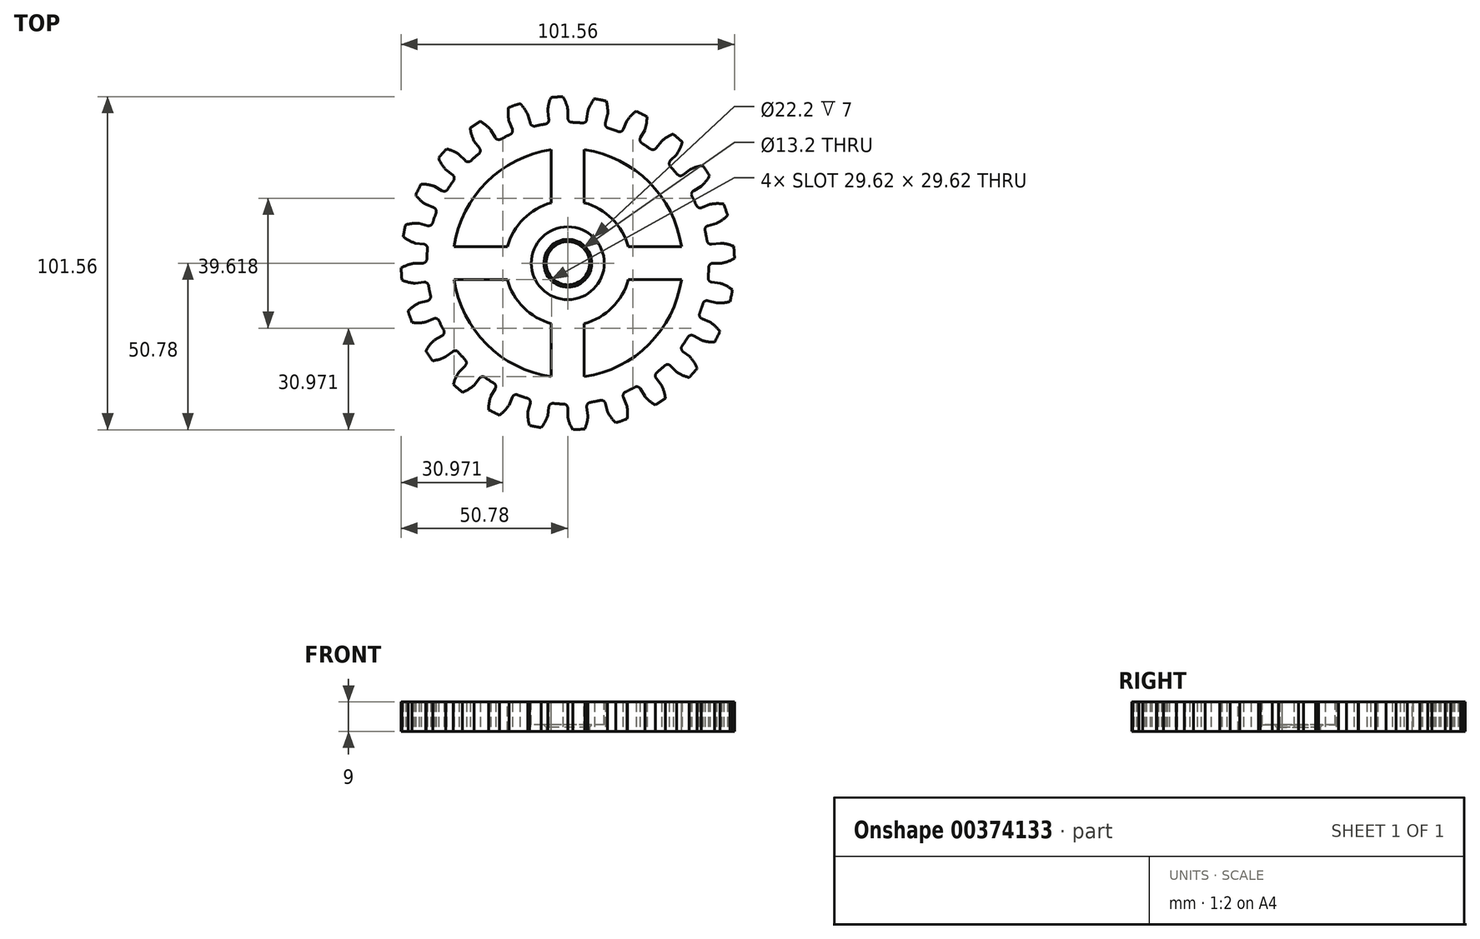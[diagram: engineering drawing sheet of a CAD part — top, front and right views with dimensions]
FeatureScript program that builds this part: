
annotation { "Feature Type Name" : "Feature", "Feature Type Description" : "" }
export const myFeature = defineFeature(function(context is Context, id is Id, definition is map)
    precondition{}
    {
        {
            var Q0;
            Q0=qCreatedBy(makeId("Top.planeOp"),FACE);
            var sketch = newSketch(context, id + "F0", { "sketchPlane" : qUnion([Q0])});
            skArc(sketch, "E0", {"start": v(-1.49, 50.78) * mm, "mid": v(-3.32, 50.7) * mm, "end": v(-5.15, 50.54) * mm});
            skCircle(sketch, "E1", {"center": v(0, 0) * mm, "radius": 42.98 * mm});
            skLineSegment(sketch, "E2", {"start": v(0, 42.98) * mm, "end": v(0, 46.89) * mm});
            skLineSegment(sketch, "E3", {"start": v(-5.6, 42.6) * mm, "end": v(-6.12, 46.49) * mm});
            skArc(sketch, "E4.trimOffspring", {"start": v(0, 46.89) * mm, "mid": v(-0.57, 48.9) * mm, "end": v(-1.49, 50.78) * mm});
            skArc(sketch, "E5.MirrorCS", {"start": v(-6.12, 46.49) * mm, "mid": v(-5.82, 48.56) * mm, "end": v(-5.15, 50.54) * mm});
            skArc(sketch, "E6.1.0", {"start": v(-12.14, 45.3) * mm, "mid": v(-13.2, 47.09) * mm, "end": v(-14.58, 48.66) * mm});
            skArc(sketch, "E6.1.1", {"start": v(-14.58, 48.66) * mm, "mid": v(-16.33, 48.1) * mm, "end": v(-18.06, 47.48) * mm});
            skArc(sketch, "E6.1.2", {"start": v(-17.94, 43.32) * mm, "mid": v(-18.19, 45.4) * mm, "end": v(-18.06, 47.48) * mm});
            skLineSegment(sketch, "E6.1.3", {"start": v(-11.12, 41.51) * mm, "end": v(-12.14, 45.3) * mm});
            skLineSegment(sketch, "E6.1.4", {"start": v(-16.45, 39.7) * mm, "end": v(-17.94, 43.32) * mm});
            skArc(sketch, "E6.2.0", {"start": v(-23.44, 40.6) * mm, "mid": v(-24.94, 42.06) * mm, "end": v(-26.68, 43.23) * mm});
            skArc(sketch, "E6.2.1", {"start": v(-26.68, 43.23) * mm, "mid": v(-28.22, 42.24) * mm, "end": v(-29.73, 41.19) * mm});
            skArc(sketch, "E6.2.2", {"start": v(-28.54, 37.2) * mm, "mid": v(-29.32, 39.14) * mm, "end": v(-29.73, 41.19) * mm});
            skLineSegment(sketch, "E6.2.3", {"start": v(-21.49, 37.22) * mm, "end": v(-23.44, 40.6) * mm});
            skLineSegment(sketch, "E6.2.4", {"start": v(-26.16, 34.1) * mm, "end": v(-28.54, 37.2) * mm});
            skArc(sketch, "E6.3.0", {"start": v(-33.16, 33.16) * mm, "mid": v(-34.98, 34.18) * mm, "end": v(-36.96, 34.85) * mm});
            skArc(sketch, "E6.3.1", {"start": v(-36.96, 34.85) * mm, "mid": v(-38.2, 33.5) * mm, "end": v(-39.38, 32.1) * mm});
            skArc(sketch, "E6.3.2", {"start": v(-37.2, 28.54) * mm, "mid": v(-38.45, 30.22) * mm, "end": v(-39.38, 32.1) * mm});
            skLineSegment(sketch, "E6.3.3", {"start": v(-30.39, 30.39) * mm, "end": v(-33.16, 33.16) * mm});
            skLineSegment(sketch, "E6.3.4", {"start": v(-34.1, 26.16) * mm, "end": v(-37.2, 28.54) * mm});
            skArc(sketch, "E6.4.0", {"start": v(-40.6, 23.44) * mm, "mid": v(-42.63, 23.96) * mm, "end": v(-44.72, 24.1) * mm});
            skArc(sketch, "E6.4.1", {"start": v(-44.72, 24.1) * mm, "mid": v(-45.56, 22.47) * mm, "end": v(-46.34, 20.8) * mm});
            skArc(sketch, "E6.4.2", {"start": v(-43.32, 17.94) * mm, "mid": v(-44.96, 19.24) * mm, "end": v(-46.34, 20.8) * mm});
            skLineSegment(sketch, "E6.4.3", {"start": v(-37.22, 21.49) * mm, "end": v(-40.6, 23.44) * mm});
            skLineSegment(sketch, "E6.4.4", {"start": v(-39.7, 16.45) * mm, "end": v(-43.32, 17.94) * mm});
            skArc(sketch, "E6.5.0", {"start": v(-45.3, 12.14) * mm, "mid": v(-47.38, 12.1) * mm, "end": v(-49.43, 11.7) * mm});
            skArc(sketch, "E6.5.1", {"start": v(-49.43, 11.7) * mm, "mid": v(-49.82, 9.91) * mm, "end": v(-50.15, 8.1) * mm});
            skArc(sketch, "E6.5.2", {"start": v(-46.49, 6.12) * mm, "mid": v(-48.4, 6.95) * mm, "end": v(-50.15, 8.1) * mm});
            skLineSegment(sketch, "E6.5.3", {"start": v(-41.51, 11.12) * mm, "end": v(-45.3, 12.14) * mm});
            skLineSegment(sketch, "E6.5.4", {"start": v(-42.6, 5.6) * mm, "end": v(-46.49, 6.12) * mm});
            skArc(sketch, "E6.6.0", {"start": v(-46.89, 0) * mm, "mid": v(-48.9, -0.57) * mm, "end": v(-50.78, -1.49) * mm});
            skArc(sketch, "E6.6.1", {"start": v(-50.78, -1.49) * mm, "mid": v(-50.7, -3.32) * mm, "end": v(-50.54, -5.15) * mm});
            skArc(sketch, "E6.6.2", {"start": v(-46.49, -6.12) * mm, "mid": v(-48.56, -5.82) * mm, "end": v(-50.54, -5.15) * mm});
            skLineSegment(sketch, "E6.6.3", {"start": v(-42.98, 0) * mm, "end": v(-46.89, 0) * mm});
            skLineSegment(sketch, "E6.6.4", {"start": v(-42.6, -5.6) * mm, "end": v(-46.49, -6.12) * mm});
            skArc(sketch, "E6.7.0", {"start": v(-45.3, -12.14) * mm, "mid": v(-47.09, -13.2) * mm, "end": v(-48.66, -14.58) * mm});
            skArc(sketch, "E6.7.1", {"start": v(-48.66, -14.58) * mm, "mid": v(-48.1, -16.33) * mm, "end": v(-47.48, -18.06) * mm});
            skArc(sketch, "E6.7.2", {"start": v(-43.32, -17.94) * mm, "mid": v(-45.4, -18.19) * mm, "end": v(-47.48, -18.06) * mm});
            skLineSegment(sketch, "E6.7.3", {"start": v(-41.51, -11.12) * mm, "end": v(-45.3, -12.14) * mm});
            skLineSegment(sketch, "E6.7.4", {"start": v(-39.7, -16.45) * mm, "end": v(-43.32, -17.94) * mm});
            skArc(sketch, "E6.8.0", {"start": v(-40.6, -23.44) * mm, "mid": v(-42.06, -24.94) * mm, "end": v(-43.23, -26.68) * mm});
            skArc(sketch, "E6.8.1", {"start": v(-43.23, -26.68) * mm, "mid": v(-42.24, -28.22) * mm, "end": v(-41.19, -29.73) * mm});
            skArc(sketch, "E6.8.2", {"start": v(-37.2, -28.54) * mm, "mid": v(-39.14, -29.32) * mm, "end": v(-41.19, -29.73) * mm});
            skLineSegment(sketch, "E6.8.3", {"start": v(-37.22, -21.49) * mm, "end": v(-40.6, -23.44) * mm});
            skLineSegment(sketch, "E6.8.4", {"start": v(-34.1, -26.16) * mm, "end": v(-37.2, -28.54) * mm});
            skArc(sketch, "E6.9.0", {"start": v(-33.16, -33.16) * mm, "mid": v(-34.18, -34.98) * mm, "end": v(-34.85, -36.96) * mm});
            skArc(sketch, "E6.9.1", {"start": v(-34.85, -36.96) * mm, "mid": v(-33.5, -38.2) * mm, "end": v(-32.1, -39.38) * mm});
            skArc(sketch, "E6.9.2", {"start": v(-28.54, -37.2) * mm, "mid": v(-30.22, -38.45) * mm, "end": v(-32.1, -39.38) * mm});
            skLineSegment(sketch, "E6.9.3", {"start": v(-30.39, -30.39) * mm, "end": v(-33.16, -33.16) * mm});
            skLineSegment(sketch, "E6.9.4", {"start": v(-26.16, -34.1) * mm, "end": v(-28.54, -37.2) * mm});
            skArc(sketch, "E6.10.0", {"start": v(-23.44, -40.6) * mm, "mid": v(-23.96, -42.63) * mm, "end": v(-24.1, -44.72) * mm});
            skArc(sketch, "E6.10.1", {"start": v(-24.1, -44.72) * mm, "mid": v(-22.47, -45.56) * mm, "end": v(-20.8, -46.34) * mm});
            skArc(sketch, "E6.10.2", {"start": v(-17.94, -43.32) * mm, "mid": v(-19.24, -44.96) * mm, "end": v(-20.8, -46.34) * mm});
            skLineSegment(sketch, "E6.10.3", {"start": v(-21.49, -37.22) * mm, "end": v(-23.44, -40.6) * mm});
            skLineSegment(sketch, "E6.10.4", {"start": v(-16.45, -39.7) * mm, "end": v(-17.94, -43.32) * mm});
            skArc(sketch, "E6.11.0", {"start": v(-12.14, -45.3) * mm, "mid": v(-12.1, -47.38) * mm, "end": v(-11.7, -49.43) * mm});
            skArc(sketch, "E6.11.1", {"start": v(-11.7, -49.43) * mm, "mid": v(-9.91, -49.82) * mm, "end": v(-8.1, -50.15) * mm});
            skArc(sketch, "E6.11.2", {"start": v(-6.12, -46.49) * mm, "mid": v(-6.95, -48.4) * mm, "end": v(-8.1, -50.15) * mm});
            skLineSegment(sketch, "E6.11.3", {"start": v(-11.12, -41.51) * mm, "end": v(-12.14, -45.3) * mm});
            skLineSegment(sketch, "E6.11.4", {"start": v(-5.6, -42.6) * mm, "end": v(-6.12, -46.49) * mm});
            skArc(sketch, "E6.12.0", {"start": v(0, -46.89) * mm, "mid": v(0.57, -48.9) * mm, "end": v(1.49, -50.78) * mm});
            skArc(sketch, "E6.12.1", {"start": v(1.49, -50.78) * mm, "mid": v(3.32, -50.7) * mm, "end": v(5.15, -50.54) * mm});
            skArc(sketch, "E6.12.2", {"start": v(6.12, -46.49) * mm, "mid": v(5.82, -48.56) * mm, "end": v(5.15, -50.54) * mm});
            skLineSegment(sketch, "E6.12.3", {"start": v(0, -42.98) * mm, "end": v(0, -46.89) * mm});
            skLineSegment(sketch, "E6.12.4", {"start": v(5.6, -42.6) * mm, "end": v(6.12, -46.49) * mm});
            skArc(sketch, "E6.13.0", {"start": v(12.14, -45.3) * mm, "mid": v(13.2, -47.09) * mm, "end": v(14.58, -48.66) * mm});
            skArc(sketch, "E6.13.1", {"start": v(14.58, -48.66) * mm, "mid": v(16.33, -48.1) * mm, "end": v(18.06, -47.48) * mm});
            skArc(sketch, "E6.13.2", {"start": v(17.94, -43.32) * mm, "mid": v(18.19, -45.4) * mm, "end": v(18.06, -47.48) * mm});
            skLineSegment(sketch, "E6.13.3", {"start": v(11.12, -41.51) * mm, "end": v(12.14, -45.3) * mm});
            skLineSegment(sketch, "E6.13.4", {"start": v(16.45, -39.7) * mm, "end": v(17.94, -43.32) * mm});
            skArc(sketch, "E6.14.0", {"start": v(23.44, -40.6) * mm, "mid": v(24.94, -42.06) * mm, "end": v(26.68, -43.23) * mm});
            skArc(sketch, "E6.14.1", {"start": v(26.68, -43.23) * mm, "mid": v(28.22, -42.24) * mm, "end": v(29.73, -41.19) * mm});
            skArc(sketch, "E6.14.2", {"start": v(28.54, -37.2) * mm, "mid": v(29.32, -39.14) * mm, "end": v(29.73, -41.19) * mm});
            skLineSegment(sketch, "E6.14.3", {"start": v(21.49, -37.22) * mm, "end": v(23.44, -40.6) * mm});
            skLineSegment(sketch, "E6.14.4", {"start": v(26.16, -34.1) * mm, "end": v(28.54, -37.2) * mm});
            skArc(sketch, "E6.15.0", {"start": v(33.16, -33.16) * mm, "mid": v(34.98, -34.18) * mm, "end": v(36.96, -34.85) * mm});
            skArc(sketch, "E6.15.1", {"start": v(36.96, -34.85) * mm, "mid": v(38.2, -33.5) * mm, "end": v(39.38, -32.1) * mm});
            skArc(sketch, "E6.15.2", {"start": v(37.2, -28.54) * mm, "mid": v(38.45, -30.22) * mm, "end": v(39.38, -32.1) * mm});
            skLineSegment(sketch, "E6.15.3", {"start": v(30.39, -30.39) * mm, "end": v(33.16, -33.16) * mm});
            skLineSegment(sketch, "E6.15.4", {"start": v(34.1, -26.16) * mm, "end": v(37.2, -28.54) * mm});
            skArc(sketch, "E6.16.0", {"start": v(40.6, -23.44) * mm, "mid": v(42.63, -23.96) * mm, "end": v(44.72, -24.1) * mm});
            skArc(sketch, "E6.16.1", {"start": v(44.72, -24.1) * mm, "mid": v(45.56, -22.47) * mm, "end": v(46.34, -20.8) * mm});
            skArc(sketch, "E6.16.2", {"start": v(43.32, -17.94) * mm, "mid": v(44.96, -19.24) * mm, "end": v(46.34, -20.8) * mm});
            skLineSegment(sketch, "E6.16.3", {"start": v(37.22, -21.49) * mm, "end": v(40.6, -23.44) * mm});
            skLineSegment(sketch, "E6.16.4", {"start": v(39.7, -16.45) * mm, "end": v(43.32, -17.94) * mm});
            skArc(sketch, "E6.17.0", {"start": v(45.3, -12.14) * mm, "mid": v(47.38, -12.1) * mm, "end": v(49.43, -11.7) * mm});
            skArc(sketch, "E6.17.1", {"start": v(49.43, -11.7) * mm, "mid": v(49.82, -9.91) * mm, "end": v(50.15, -8.1) * mm});
            skArc(sketch, "E6.17.2", {"start": v(46.49, -6.12) * mm, "mid": v(48.4, -6.95) * mm, "end": v(50.15, -8.1) * mm});
            skLineSegment(sketch, "E6.17.3", {"start": v(41.51, -11.12) * mm, "end": v(45.3, -12.14) * mm});
            skLineSegment(sketch, "E6.17.4", {"start": v(42.6, -5.6) * mm, "end": v(46.49, -6.12) * mm});
            skArc(sketch, "E6.18.0", {"start": v(46.89, 0) * mm, "mid": v(48.9, 0.57) * mm, "end": v(50.78, 1.49) * mm});
            skArc(sketch, "E6.18.1", {"start": v(50.78, 1.49) * mm, "mid": v(50.7, 3.32) * mm, "end": v(50.54, 5.15) * mm});
            skArc(sketch, "E6.18.2", {"start": v(46.49, 6.12) * mm, "mid": v(48.56, 5.82) * mm, "end": v(50.54, 5.15) * mm});
            skLineSegment(sketch, "E6.18.3", {"start": v(42.98, 0) * mm, "end": v(46.89, 0) * mm});
            skLineSegment(sketch, "E6.18.4", {"start": v(42.6, 5.6) * mm, "end": v(46.49, 6.12) * mm});
            skArc(sketch, "E6.19.0", {"start": v(45.3, 12.14) * mm, "mid": v(47.09, 13.2) * mm, "end": v(48.66, 14.58) * mm});
            skArc(sketch, "E6.19.1", {"start": v(48.66, 14.58) * mm, "mid": v(48.1, 16.33) * mm, "end": v(47.48, 18.06) * mm});
            skArc(sketch, "E6.19.2", {"start": v(43.32, 17.94) * mm, "mid": v(45.4, 18.19) * mm, "end": v(47.48, 18.06) * mm});
            skLineSegment(sketch, "E6.19.3", {"start": v(41.51, 11.12) * mm, "end": v(45.3, 12.14) * mm});
            skLineSegment(sketch, "E6.19.4", {"start": v(39.7, 16.45) * mm, "end": v(43.32, 17.94) * mm});
            skArc(sketch, "E6.20.0", {"start": v(40.6, 23.44) * mm, "mid": v(42.06, 24.94) * mm, "end": v(43.23, 26.68) * mm});
            skArc(sketch, "E6.20.1", {"start": v(43.23, 26.68) * mm, "mid": v(42.24, 28.22) * mm, "end": v(41.19, 29.73) * mm});
            skArc(sketch, "E6.20.2", {"start": v(37.2, 28.54) * mm, "mid": v(39.14, 29.32) * mm, "end": v(41.19, 29.73) * mm});
            skLineSegment(sketch, "E6.20.3", {"start": v(37.22, 21.49) * mm, "end": v(40.6, 23.44) * mm});
            skLineSegment(sketch, "E6.20.4", {"start": v(34.1, 26.16) * mm, "end": v(37.2, 28.54) * mm});
            skArc(sketch, "E6.21.0", {"start": v(33.16, 33.16) * mm, "mid": v(34.18, 34.98) * mm, "end": v(34.85, 36.96) * mm});
            skArc(sketch, "E6.21.1", {"start": v(34.85, 36.96) * mm, "mid": v(33.5, 38.2) * mm, "end": v(32.1, 39.38) * mm});
            skArc(sketch, "E6.21.2", {"start": v(28.54, 37.2) * mm, "mid": v(30.22, 38.45) * mm, "end": v(32.1, 39.38) * mm});
            skLineSegment(sketch, "E6.21.3", {"start": v(30.39, 30.39) * mm, "end": v(33.16, 33.16) * mm});
            skLineSegment(sketch, "E6.21.4", {"start": v(26.16, 34.1) * mm, "end": v(28.54, 37.2) * mm});
            skArc(sketch, "E6.22.0", {"start": v(23.44, 40.6) * mm, "mid": v(23.96, 42.63) * mm, "end": v(24.1, 44.72) * mm});
            skArc(sketch, "E6.22.1", {"start": v(24.1, 44.72) * mm, "mid": v(22.47, 45.56) * mm, "end": v(20.8, 46.34) * mm});
            skArc(sketch, "E6.22.2", {"start": v(17.94, 43.32) * mm, "mid": v(19.24, 44.96) * mm, "end": v(20.8, 46.34) * mm});
            skLineSegment(sketch, "E6.22.3", {"start": v(21.49, 37.22) * mm, "end": v(23.44, 40.6) * mm});
            skLineSegment(sketch, "E6.22.4", {"start": v(16.45, 39.7) * mm, "end": v(17.94, 43.32) * mm});
            skArc(sketch, "E6.23.0", {"start": v(12.14, 45.3) * mm, "mid": v(12.1, 47.38) * mm, "end": v(11.7, 49.43) * mm});
            skArc(sketch, "E6.23.1", {"start": v(11.7, 49.43) * mm, "mid": v(9.91, 49.82) * mm, "end": v(8.1, 50.15) * mm});
            skArc(sketch, "E6.23.2", {"start": v(6.12, 46.49) * mm, "mid": v(6.95, 48.4) * mm, "end": v(8.1, 50.15) * mm});
            skLineSegment(sketch, "E6.23.3", {"start": v(11.12, 41.51) * mm, "end": v(12.14, 45.3) * mm});
            skLineSegment(sketch, "E6.23.4", {"start": v(5.6, 42.6) * mm, "end": v(6.12, 46.49) * mm});
            skSolve(sketch);
        }
        {
            var Q0;
            Q0 = qSketchRegion(id + "F0", true);
            extrude(context, id + "F1", {"entities" : qUnion([Q0]), "depth" : 9 * mm});
        }
        {
            var Q0;
            Q0=makeQuery(id+"F1.opExtrude","SWEPT_EDGE",EDGE,{"disambiguationData":[OSD([sQuery(id+"F0.wireOp",EDGE,"E1"),sQuery(id+"F0.wireOp",EDGE,"E6.4.4")])]});
            var Q1;
            Q1=makeQuery(id+"F1.opExtrude","SWEPT_EDGE",EDGE,{"disambiguationData":[OSD([sQuery(id+"F0.wireOp",EDGE,"E1"),sQuery(id+"F0.wireOp",EDGE,"E6.5.3")])]});
            var Q2;
            Q2=makeQuery(id+"F1.opExtrude","SWEPT_EDGE",EDGE,{"disambiguationData":[OSD([sQuery(id+"F0.wireOp",EDGE,"E1"),sQuery(id+"F0.wireOp",EDGE,"E6.4.3")])]});
            var Q3;
            Q3=makeQuery(id+"F1.opExtrude","SWEPT_EDGE",EDGE,{"disambiguationData":[OSD([sQuery(id+"F0.wireOp",EDGE,"E1"),sQuery(id+"F0.wireOp",EDGE,"E6.3.4")])]});
            var Q4;
            Q4=makeQuery(id+"F1.opExtrude","SWEPT_EDGE",EDGE,{"disambiguationData":[OSD([sQuery(id+"F0.wireOp",EDGE,"E1"),sQuery(id+"F0.wireOp",EDGE,"E6.2.4")])]});
            var Q5;
            Q5=makeQuery(id+"F1.opExtrude","SWEPT_EDGE",EDGE,{"disambiguationData":[OSD([sQuery(id+"F0.wireOp",EDGE,"E1"),sQuery(id+"F0.wireOp",EDGE,"E6.3.3")])]});
            var Q6;
            Q6=makeQuery(id+"F1.opExtrude","SWEPT_EDGE",EDGE,{"disambiguationData":[OSD([sQuery(id+"F0.wireOp",EDGE,"E1"),sQuery(id+"F0.wireOp",EDGE,"E6.2.3")])]});
            var Q7;
            Q7=makeQuery(id+"F1.opExtrude","SWEPT_EDGE",EDGE,{"disambiguationData":[OSD([sQuery(id+"F0.wireOp",EDGE,"E1"),sQuery(id+"F0.wireOp",EDGE,"E6.1.4")])]});
            var Q8;
            Q8=makeQuery(id+"F1.opExtrude","SWEPT_EDGE",EDGE,{"disambiguationData":[OSD([sQuery(id+"F0.wireOp",EDGE,"E1"),sQuery(id+"F0.wireOp",EDGE,"E3")])]});
            var Q9;
            Q9=makeQuery(id+"F1.opExtrude","SWEPT_EDGE",EDGE,{"disambiguationData":[OSD([sQuery(id+"F0.wireOp",EDGE,"E1"),sQuery(id+"F0.wireOp",EDGE,"E6.1.3")])]});
            var Q10;
            Q10=makeQuery(id+"F1.opExtrude","SWEPT_EDGE",EDGE,{"disambiguationData":[OSD([sQuery(id+"F0.wireOp",EDGE,"E1"),sQuery(id+"F0.wireOp",EDGE,"E2")])]});
            var Q11;
            Q11=makeQuery(id+"F1.opExtrude","SWEPT_EDGE",EDGE,{"disambiguationData":[OSD([sQuery(id+"F0.wireOp",EDGE,"E1"),sQuery(id+"F0.wireOp",EDGE,"E6.23.4")])]});
            var Q12;
            Q12=makeQuery(id+"F1.opExtrude","SWEPT_EDGE",EDGE,{"disambiguationData":[OSD([sQuery(id+"F0.wireOp",EDGE,"E1"),sQuery(id+"F0.wireOp",EDGE,"E6.23.3")])]});
            var Q13;
            Q13=makeQuery(id+"F1.opExtrude","SWEPT_EDGE",EDGE,{"disambiguationData":[OSD([sQuery(id+"F0.wireOp",EDGE,"E1"),sQuery(id+"F0.wireOp",EDGE,"E6.22.4")])]});
            var Q14;
            Q14=makeQuery(id+"F1.opExtrude","SWEPT_EDGE",EDGE,{"disambiguationData":[OSD([sQuery(id+"F0.wireOp",EDGE,"E1"),sQuery(id+"F0.wireOp",EDGE,"E6.22.3")])]});
            var Q15;
            Q15=makeQuery(id+"F1.opExtrude","SWEPT_EDGE",EDGE,{"disambiguationData":[OSD([sQuery(id+"F0.wireOp",EDGE,"E1"),sQuery(id+"F0.wireOp",EDGE,"E6.21.4")])]});
            var Q16;
            Q16=makeQuery(id+"F1.opExtrude","SWEPT_EDGE",EDGE,{"disambiguationData":[OSD([sQuery(id+"F0.wireOp",EDGE,"E1"),sQuery(id+"F0.wireOp",EDGE,"E6.21.3")])]});
            var Q17;
            Q17=makeQuery(id+"F1.opExtrude","SWEPT_EDGE",EDGE,{"disambiguationData":[OSD([sQuery(id+"F0.wireOp",EDGE,"E1"),sQuery(id+"F0.wireOp",EDGE,"E6.20.4")])]});
            var Q18;
            Q18=makeQuery(id+"F1.opExtrude","SWEPT_EDGE",EDGE,{"disambiguationData":[OSD([sQuery(id+"F0.wireOp",EDGE,"E1"),sQuery(id+"F0.wireOp",EDGE,"E6.20.3")])]});
            var Q19;
            Q19=makeQuery(id+"F1.opExtrude","SWEPT_EDGE",EDGE,{"disambiguationData":[OSD([sQuery(id+"F0.wireOp",EDGE,"E1"),sQuery(id+"F0.wireOp",EDGE,"E6.19.3")])]});
            var Q20;
            Q20=makeQuery(id+"F1.opExtrude","SWEPT_EDGE",EDGE,{"disambiguationData":[OSD([sQuery(id+"F0.wireOp",EDGE,"E1"),sQuery(id+"F0.wireOp",EDGE,"E6.19.4")])]});
            var Q21;
            Q21=makeQuery(id+"F1.opExtrude","SWEPT_EDGE",EDGE,{"disambiguationData":[OSD([sQuery(id+"F0.wireOp",EDGE,"E1"),sQuery(id+"F0.wireOp",EDGE,"E6.18.4")])]});
            var Q22;
            Q22=makeQuery(id+"F1.opExtrude","SWEPT_EDGE",EDGE,{"disambiguationData":[OSD([sQuery(id+"F0.wireOp",EDGE,"E1"),sQuery(id+"F0.wireOp",EDGE,"E6.17.4")])]});
            var Q23;
            Q23=makeQuery(id+"F1.opExtrude","SWEPT_EDGE",EDGE,{"disambiguationData":[OSD([sQuery(id+"F0.wireOp",EDGE,"E1"),sQuery(id+"F0.wireOp",EDGE,"E6.18.3")])]});
            var Q24;
            Q24=makeQuery(id+"F1.opExtrude","SWEPT_EDGE",EDGE,{"disambiguationData":[OSD([sQuery(id+"F0.wireOp",EDGE,"E1"),sQuery(id+"F0.wireOp",EDGE,"E6.17.3")])]});
            var Q25;
            Q25=makeQuery(id+"F1.opExtrude","SWEPT_EDGE",EDGE,{"disambiguationData":[OSD([sQuery(id+"F0.wireOp",EDGE,"E1"),sQuery(id+"F0.wireOp",EDGE,"E6.16.3")])]});
            var Q26;
            Q26=makeQuery(id+"F1.opExtrude","SWEPT_EDGE",EDGE,{"disambiguationData":[OSD([sQuery(id+"F0.wireOp",EDGE,"E1"),sQuery(id+"F0.wireOp",EDGE,"E6.15.3")])]});
            var Q27;
            Q27=makeQuery(id+"F1.opExtrude","SWEPT_EDGE",EDGE,{"disambiguationData":[OSD([sQuery(id+"F0.wireOp",EDGE,"E1"),sQuery(id+"F0.wireOp",EDGE,"E6.16.4")])]});
            var Q28;
            Q28=makeQuery(id+"F1.opExtrude","SWEPT_EDGE",EDGE,{"disambiguationData":[OSD([sQuery(id+"F0.wireOp",EDGE,"E1"),sQuery(id+"F0.wireOp",EDGE,"E6.15.4")])]});
            var Q29;
            Q29=makeQuery(id+"F1.opExtrude","SWEPT_EDGE",EDGE,{"disambiguationData":[OSD([sQuery(id+"F0.wireOp",EDGE,"E1"),sQuery(id+"F0.wireOp",EDGE,"E6.14.4")])]});
            var Q30;
            Q30=makeQuery(id+"F1.opExtrude","SWEPT_EDGE",EDGE,{"disambiguationData":[OSD([sQuery(id+"F0.wireOp",EDGE,"E1"),sQuery(id+"F0.wireOp",EDGE,"E6.14.3")])]});
            var Q31;
            Q31=makeQuery(id+"F1.opExtrude","SWEPT_EDGE",EDGE,{"disambiguationData":[OSD([sQuery(id+"F0.wireOp",EDGE,"E1"),sQuery(id+"F0.wireOp",EDGE,"E6.13.4")])]});
            var Q32;
            Q32=makeQuery(id+"F1.opExtrude","SWEPT_EDGE",EDGE,{"disambiguationData":[OSD([sQuery(id+"F0.wireOp",EDGE,"E1"),sQuery(id+"F0.wireOp",EDGE,"E6.13.3")])]});
            var Q33;
            Q33=makeQuery(id+"F1.opExtrude","SWEPT_EDGE",EDGE,{"disambiguationData":[OSD([sQuery(id+"F0.wireOp",EDGE,"E1"),sQuery(id+"F0.wireOp",EDGE,"E6.12.4")])]});
            var Q34;
            Q34=makeQuery(id+"F1.opExtrude","SWEPT_EDGE",EDGE,{"disambiguationData":[OSD([sQuery(id+"F0.wireOp",EDGE,"E1"),sQuery(id+"F0.wireOp",EDGE,"E6.12.3")])]});
            var Q35;
            Q35=makeQuery(id+"F1.opExtrude","SWEPT_EDGE",EDGE,{"disambiguationData":[OSD([sQuery(id+"F0.wireOp",EDGE,"E1"),sQuery(id+"F0.wireOp",EDGE,"E6.11.4")])]});
            var Q36;
            Q36=makeQuery(id+"F1.opExtrude","SWEPT_EDGE",EDGE,{"disambiguationData":[OSD([sQuery(id+"F0.wireOp",EDGE,"E1"),sQuery(id+"F0.wireOp",EDGE,"E6.11.3")])]});
            var Q37;
            Q37=makeQuery(id+"F1.opExtrude","SWEPT_EDGE",EDGE,{"disambiguationData":[OSD([sQuery(id+"F0.wireOp",EDGE,"E1"),sQuery(id+"F0.wireOp",EDGE,"E6.10.4")])]});
            var Q38;
            Q38=makeQuery(id+"F1.opExtrude","SWEPT_EDGE",EDGE,{"disambiguationData":[OSD([sQuery(id+"F0.wireOp",EDGE,"E1"),sQuery(id+"F0.wireOp",EDGE,"E6.10.3")])]});
            var Q39;
            Q39=makeQuery(id+"F1.opExtrude","SWEPT_EDGE",EDGE,{"disambiguationData":[OSD([sQuery(id+"F0.wireOp",EDGE,"E1"),sQuery(id+"F0.wireOp",EDGE,"E6.9.4")])]});
            var Q40;
            Q40=makeQuery(id+"F1.opExtrude","SWEPT_EDGE",EDGE,{"disambiguationData":[OSD([sQuery(id+"F0.wireOp",EDGE,"E1"),sQuery(id+"F0.wireOp",EDGE,"E6.9.3")])]});
            var Q41;
            Q41=makeQuery(id+"F1.opExtrude","SWEPT_EDGE",EDGE,{"disambiguationData":[OSD([sQuery(id+"F0.wireOp",EDGE,"E1"),sQuery(id+"F0.wireOp",EDGE,"E6.8.3")])]});
            var Q42;
            Q42=makeQuery(id+"F1.opExtrude","SWEPT_EDGE",EDGE,{"disambiguationData":[OSD([sQuery(id+"F0.wireOp",EDGE,"E1"),sQuery(id+"F0.wireOp",EDGE,"E6.7.3")])]});
            var Q43;
            Q43=makeQuery(id+"F1.opExtrude","SWEPT_EDGE",EDGE,{"disambiguationData":[OSD([sQuery(id+"F0.wireOp",EDGE,"E1"),sQuery(id+"F0.wireOp",EDGE,"E6.8.4")])]});
            var Q44;
            Q44=makeQuery(id+"F1.opExtrude","SWEPT_EDGE",EDGE,{"disambiguationData":[OSD([sQuery(id+"F0.wireOp",EDGE,"E1"),sQuery(id+"F0.wireOp",EDGE,"E6.7.4")])]});
            var Q45;
            Q45=makeQuery(id+"F1.opExtrude","SWEPT_EDGE",EDGE,{"disambiguationData":[OSD([sQuery(id+"F0.wireOp",EDGE,"E1"),sQuery(id+"F0.wireOp",EDGE,"E6.6.4")])]});
            var Q46;
            Q46=makeQuery(id+"F1.opExtrude","SWEPT_EDGE",EDGE,{"disambiguationData":[OSD([sQuery(id+"F0.wireOp",EDGE,"E1"),sQuery(id+"F0.wireOp",EDGE,"E6.5.4")])]});
            var Q47;
            Q47=makeQuery(id+"F1.opExtrude","SWEPT_EDGE",EDGE,{"disambiguationData":[OSD([sQuery(id+"F0.wireOp",EDGE,"E1"),sQuery(id+"F0.wireOp",EDGE,"E6.6.3")])]});
            fillet(context, id + "F2", {"entities" : qUnion([Q0, Q1, Q2, Q3, Q4, Q5, Q6, Q7, Q8, Q9, Q10, Q11, Q12, Q13, Q14, Q15, Q16, Q17, Q18, Q19, Q20, Q21, Q22, Q23, Q24, Q25, Q26, Q27, Q28, Q29, Q30, Q31, Q32, Q33, Q34, Q35, Q36, Q37, Q38, Q39, Q40, Q41, Q42, Q43, Q44, Q45, Q46, Q47]), "radius" : 1.27 * mm, "tangentPropagation" : true, "allowEdgeOverflow" : false});
        }
        {
            var Q0;
            Q0=makeQuery(id+"F1.opExtrude","CAP_FACE",FACE,{"disambiguationData":[OSD([sQuery(id+"F0.wireOp",EDGE,"E0"),sQuery(id+"F0.wireOp",EDGE,"E1"),sQuery(id+"F0.wireOp",EDGE,"E2"),sQuery(id+"F0.wireOp",EDGE,"E3"),sQuery(id+"F0.wireOp",EDGE,"E4.trimOffspring"),sQuery(id+"F0.wireOp",EDGE,"E5.MirrorCS"),sQuery(id+"F0.wireOp",EDGE,"E6.1.0"),sQuery(id+"F0.wireOp",EDGE,"E6.1.1"),sQuery(id+"F0.wireOp",EDGE,"E6.1.2"),sQuery(id+"F0.wireOp",EDGE,"E6.1.3"),sQuery(id+"F0.wireOp",EDGE,"E6.1.4"),sQuery(id+"F0.wireOp",EDGE,"E6.2.0"),sQuery(id+"F0.wireOp",EDGE,"E6.2.1"),sQuery(id+"F0.wireOp",EDGE,"E6.2.2"),sQuery(id+"F0.wireOp",EDGE,"E6.2.3"),sQuery(id+"F0.wireOp",EDGE,"E6.2.4"),sQuery(id+"F0.wireOp",EDGE,"E6.3.0"),sQuery(id+"F0.wireOp",EDGE,"E6.3.1"),sQuery(id+"F0.wireOp",EDGE,"E6.3.2"),sQuery(id+"F0.wireOp",EDGE,"E6.3.3"),sQuery(id+"F0.wireOp",EDGE,"E6.3.4"),sQuery(id+"F0.wireOp",EDGE,"E6.4.0"),sQuery(id+"F0.wireOp",EDGE,"E6.4.1"),sQuery(id+"F0.wireOp",EDGE,"E6.4.2"),sQuery(id+"F0.wireOp",EDGE,"E6.4.3"),sQuery(id+"F0.wireOp",EDGE,"E6.4.4"),sQuery(id+"F0.wireOp",EDGE,"E6.5.0"),sQuery(id+"F0.wireOp",EDGE,"E6.5.1"),sQuery(id+"F0.wireOp",EDGE,"E6.5.2"),sQuery(id+"F0.wireOp",EDGE,"E6.5.3"),sQuery(id+"F0.wireOp",EDGE,"E6.5.4"),sQuery(id+"F0.wireOp",EDGE,"E6.6.0"),sQuery(id+"F0.wireOp",EDGE,"E6.6.1"),sQuery(id+"F0.wireOp",EDGE,"E6.6.2"),sQuery(id+"F0.wireOp",EDGE,"E6.6.3"),sQuery(id+"F0.wireOp",EDGE,"E6.6.4"),sQuery(id+"F0.wireOp",EDGE,"E6.7.0"),sQuery(id+"F0.wireOp",EDGE,"E6.7.1"),sQuery(id+"F0.wireOp",EDGE,"E6.7.2"),sQuery(id+"F0.wireOp",EDGE,"E6.7.3"),sQuery(id+"F0.wireOp",EDGE,"E6.7.4"),sQuery(id+"F0.wireOp",EDGE,"E6.8.0"),sQuery(id+"F0.wireOp",EDGE,"E6.8.1"),sQuery(id+"F0.wireOp",EDGE,"E6.8.2"),sQuery(id+"F0.wireOp",EDGE,"E6.8.3"),sQuery(id+"F0.wireOp",EDGE,"E6.8.4"),sQuery(id+"F0.wireOp",EDGE,"E6.9.0"),sQuery(id+"F0.wireOp",EDGE,"E6.9.1"),sQuery(id+"F0.wireOp",EDGE,"E6.9.2"),sQuery(id+"F0.wireOp",EDGE,"E6.9.3"),sQuery(id+"F0.wireOp",EDGE,"E6.9.4"),sQuery(id+"F0.wireOp",EDGE,"E6.10.0"),sQuery(id+"F0.wireOp",EDGE,"E6.10.1"),sQuery(id+"F0.wireOp",EDGE,"E6.10.2"),sQuery(id+"F0.wireOp",EDGE,"E6.10.3"),sQuery(id+"F0.wireOp",EDGE,"E6.10.4"),sQuery(id+"F0.wireOp",EDGE,"E6.11.0"),sQuery(id+"F0.wireOp",EDGE,"E6.11.1"),sQuery(id+"F0.wireOp",EDGE,"E6.11.2"),sQuery(id+"F0.wireOp",EDGE,"E6.11.3"),sQuery(id+"F0.wireOp",EDGE,"E6.11.4"),sQuery(id+"F0.wireOp",EDGE,"E6.12.0"),sQuery(id+"F0.wireOp",EDGE,"E6.12.1"),sQuery(id+"F0.wireOp",EDGE,"E6.12.2"),sQuery(id+"F0.wireOp",EDGE,"E6.12.3"),sQuery(id+"F0.wireOp",EDGE,"E6.12.4"),sQuery(id+"F0.wireOp",EDGE,"E6.13.0"),sQuery(id+"F0.wireOp",EDGE,"E6.13.1"),sQuery(id+"F0.wireOp",EDGE,"E6.13.2"),sQuery(id+"F0.wireOp",EDGE,"E6.13.3"),sQuery(id+"F0.wireOp",EDGE,"E6.13.4"),sQuery(id+"F0.wireOp",EDGE,"E6.14.0"),sQuery(id+"F0.wireOp",EDGE,"E6.14.1"),sQuery(id+"F0.wireOp",EDGE,"E6.14.2"),sQuery(id+"F0.wireOp",EDGE,"E6.14.3"),sQuery(id+"F0.wireOp",EDGE,"E6.14.4"),sQuery(id+"F0.wireOp",EDGE,"E6.15.0"),sQuery(id+"F0.wireOp",EDGE,"E6.15.1"),sQuery(id+"F0.wireOp",EDGE,"E6.15.2"),sQuery(id+"F0.wireOp",EDGE,"E6.15.3"),sQuery(id+"F0.wireOp",EDGE,"E6.15.4"),sQuery(id+"F0.wireOp",EDGE,"E6.16.0"),sQuery(id+"F0.wireOp",EDGE,"E6.16.1"),sQuery(id+"F0.wireOp",EDGE,"E6.16.2"),sQuery(id+"F0.wireOp",EDGE,"E6.16.3"),sQuery(id+"F0.wireOp",EDGE,"E6.16.4"),sQuery(id+"F0.wireOp",EDGE,"E6.17.0"),sQuery(id+"F0.wireOp",EDGE,"E6.17.1"),sQuery(id+"F0.wireOp",EDGE,"E6.17.2"),sQuery(id+"F0.wireOp",EDGE,"E6.17.3"),sQuery(id+"F0.wireOp",EDGE,"E6.17.4"),sQuery(id+"F0.wireOp",EDGE,"E6.18.0"),sQuery(id+"F0.wireOp",EDGE,"E6.18.1"),sQuery(id+"F0.wireOp",EDGE,"E6.18.2"),sQuery(id+"F0.wireOp",EDGE,"E6.18.3"),sQuery(id+"F0.wireOp",EDGE,"E6.18.4"),sQuery(id+"F0.wireOp",EDGE,"E6.19.0"),sQuery(id+"F0.wireOp",EDGE,"E6.19.1"),sQuery(id+"F0.wireOp",EDGE,"E6.19.2"),sQuery(id+"F0.wireOp",EDGE,"E6.19.3"),sQuery(id+"F0.wireOp",EDGE,"E6.19.4"),sQuery(id+"F0.wireOp",EDGE,"E6.20.0"),sQuery(id+"F0.wireOp",EDGE,"E6.20.1"),sQuery(id+"F0.wireOp",EDGE,"E6.20.2"),sQuery(id+"F0.wireOp",EDGE,"E6.20.3"),sQuery(id+"F0.wireOp",EDGE,"E6.20.4"),sQuery(id+"F0.wireOp",EDGE,"E6.21.0"),sQuery(id+"F0.wireOp",EDGE,"E6.21.1"),sQuery(id+"F0.wireOp",EDGE,"E6.21.2"),sQuery(id+"F0.wireOp",EDGE,"E6.21.3"),sQuery(id+"F0.wireOp",EDGE,"E6.21.4"),sQuery(id+"F0.wireOp",EDGE,"E6.22.0"),sQuery(id+"F0.wireOp",EDGE,"E6.22.1"),sQuery(id+"F0.wireOp",EDGE,"E6.22.2"),sQuery(id+"F0.wireOp",EDGE,"E6.22.3"),sQuery(id+"F0.wireOp",EDGE,"E6.22.4"),sQuery(id+"F0.wireOp",EDGE,"E6.23.0"),sQuery(id+"F0.wireOp",EDGE,"E6.23.1"),sQuery(id+"F0.wireOp",EDGE,"E6.23.2"),sQuery(id+"F0.wireOp",EDGE,"E6.23.3"),sQuery(id+"F0.wireOp",EDGE,"E6.23.4")])],"isStart":false});
            var sketch = newSketch(context, id + "F3", { "sketchPlane" : qUnion([Q0])});
            skCircle(sketch, "E7", {"center": v(0, 0) * mm, "radius": 11.1 * mm});
            skSolve(sketch);
        }
        {
            var Q0;
            Q0 = qSketchRegion(id + "F3", true);
            extrude(context, id + "F4", {"entities" : qUnion([Q0]), "operationType" : NewBodyOperationType.REMOVE, "oppositeDirection" : true, "depth" : 25.4 * mm});
        }
        {
            var Q0;
            Q0=qCreatedBy(makeId("Top.planeOp"),FACE);
            var sketch = newSketch(context, id + "F5", { "sketchPlane" : qUnion([Q0])});
            skCircle(sketch, "E8.0", {"center": v(0, 0) * mm, "radius": 11.1 * mm});
            skCircle(sketch, "E9.0", {"center": v(0, 0) * mm, "radius": 6.6 * mm});
            skSolve(sketch);
        }
        {
            var Q0;
            Q0=makeQuery(id+"F5.imprint","IMPRINT",FACE,{"disambiguationData":[TD([[makeQuery(id+"F5.imprint","IMPRINT",EDGE,{"derivedFrom":sQuery(id+"F5.wireOp",EDGE,"E8.0")}),1.0]])]});
            extrude(context, id + "F6", {"entities" : qUnion([Q0]), "operationType" : NewBodyOperationType.ADD, "depth" : 2 * mm});
        }
        {
            var Q0;
            Q0=makeQuery(id+"F6.opExtrude","CAP_EDGE",EDGE,{"disambiguationData":[OSD([sQuery(id+"F5.wireOp",EDGE,"E9.0")])],"isStart":false});
            chamfer(context, id + "F7", {"entities" : qUnion([Q0]), "width" : 0.7 * mm, "tangentPropagation" : true});
        }
        {
            var Q0;
            Q0=makeQuery(id+"F1.opExtrude","CAP_FACE",FACE,{"disambiguationData":[OSD([sQuery(id+"F0.wireOp",EDGE,"E0"),sQuery(id+"F0.wireOp",EDGE,"E1"),sQuery(id+"F0.wireOp",EDGE,"E2"),sQuery(id+"F0.wireOp",EDGE,"E3"),sQuery(id+"F0.wireOp",EDGE,"E4.trimOffspring"),sQuery(id+"F0.wireOp",EDGE,"E5.MirrorCS"),sQuery(id+"F0.wireOp",EDGE,"E6.1.0"),sQuery(id+"F0.wireOp",EDGE,"E6.1.1"),sQuery(id+"F0.wireOp",EDGE,"E6.1.2"),sQuery(id+"F0.wireOp",EDGE,"E6.1.3"),sQuery(id+"F0.wireOp",EDGE,"E6.1.4"),sQuery(id+"F0.wireOp",EDGE,"E6.2.0"),sQuery(id+"F0.wireOp",EDGE,"E6.2.1"),sQuery(id+"F0.wireOp",EDGE,"E6.2.2"),sQuery(id+"F0.wireOp",EDGE,"E6.2.3"),sQuery(id+"F0.wireOp",EDGE,"E6.2.4"),sQuery(id+"F0.wireOp",EDGE,"E6.3.0"),sQuery(id+"F0.wireOp",EDGE,"E6.3.1"),sQuery(id+"F0.wireOp",EDGE,"E6.3.2"),sQuery(id+"F0.wireOp",EDGE,"E6.3.3"),sQuery(id+"F0.wireOp",EDGE,"E6.3.4"),sQuery(id+"F0.wireOp",EDGE,"E6.4.0"),sQuery(id+"F0.wireOp",EDGE,"E6.4.1"),sQuery(id+"F0.wireOp",EDGE,"E6.4.2"),sQuery(id+"F0.wireOp",EDGE,"E6.4.3"),sQuery(id+"F0.wireOp",EDGE,"E6.4.4"),sQuery(id+"F0.wireOp",EDGE,"E6.5.0"),sQuery(id+"F0.wireOp",EDGE,"E6.5.1"),sQuery(id+"F0.wireOp",EDGE,"E6.5.2"),sQuery(id+"F0.wireOp",EDGE,"E6.5.3"),sQuery(id+"F0.wireOp",EDGE,"E6.5.4"),sQuery(id+"F0.wireOp",EDGE,"E6.6.0"),sQuery(id+"F0.wireOp",EDGE,"E6.6.1"),sQuery(id+"F0.wireOp",EDGE,"E6.6.2"),sQuery(id+"F0.wireOp",EDGE,"E6.6.3"),sQuery(id+"F0.wireOp",EDGE,"E6.6.4"),sQuery(id+"F0.wireOp",EDGE,"E6.7.0"),sQuery(id+"F0.wireOp",EDGE,"E6.7.1"),sQuery(id+"F0.wireOp",EDGE,"E6.7.2"),sQuery(id+"F0.wireOp",EDGE,"E6.7.3"),sQuery(id+"F0.wireOp",EDGE,"E6.7.4"),sQuery(id+"F0.wireOp",EDGE,"E6.8.0"),sQuery(id+"F0.wireOp",EDGE,"E6.8.1"),sQuery(id+"F0.wireOp",EDGE,"E6.8.2"),sQuery(id+"F0.wireOp",EDGE,"E6.8.3"),sQuery(id+"F0.wireOp",EDGE,"E6.8.4"),sQuery(id+"F0.wireOp",EDGE,"E6.9.0"),sQuery(id+"F0.wireOp",EDGE,"E6.9.1"),sQuery(id+"F0.wireOp",EDGE,"E6.9.2"),sQuery(id+"F0.wireOp",EDGE,"E6.9.3"),sQuery(id+"F0.wireOp",EDGE,"E6.9.4"),sQuery(id+"F0.wireOp",EDGE,"E6.10.0"),sQuery(id+"F0.wireOp",EDGE,"E6.10.1"),sQuery(id+"F0.wireOp",EDGE,"E6.10.2"),sQuery(id+"F0.wireOp",EDGE,"E6.10.3"),sQuery(id+"F0.wireOp",EDGE,"E6.10.4"),sQuery(id+"F0.wireOp",EDGE,"E6.11.0"),sQuery(id+"F0.wireOp",EDGE,"E6.11.1"),sQuery(id+"F0.wireOp",EDGE,"E6.11.2"),sQuery(id+"F0.wireOp",EDGE,"E6.11.3"),sQuery(id+"F0.wireOp",EDGE,"E6.11.4"),sQuery(id+"F0.wireOp",EDGE,"E6.12.0"),sQuery(id+"F0.wireOp",EDGE,"E6.12.1"),sQuery(id+"F0.wireOp",EDGE,"E6.12.2"),sQuery(id+"F0.wireOp",EDGE,"E6.12.3"),sQuery(id+"F0.wireOp",EDGE,"E6.12.4"),sQuery(id+"F0.wireOp",EDGE,"E6.13.0"),sQuery(id+"F0.wireOp",EDGE,"E6.13.1"),sQuery(id+"F0.wireOp",EDGE,"E6.13.2"),sQuery(id+"F0.wireOp",EDGE,"E6.13.3"),sQuery(id+"F0.wireOp",EDGE,"E6.13.4"),sQuery(id+"F0.wireOp",EDGE,"E6.14.0"),sQuery(id+"F0.wireOp",EDGE,"E6.14.1"),sQuery(id+"F0.wireOp",EDGE,"E6.14.2"),sQuery(id+"F0.wireOp",EDGE,"E6.14.3"),sQuery(id+"F0.wireOp",EDGE,"E6.14.4"),sQuery(id+"F0.wireOp",EDGE,"E6.15.0"),sQuery(id+"F0.wireOp",EDGE,"E6.15.1"),sQuery(id+"F0.wireOp",EDGE,"E6.15.2"),sQuery(id+"F0.wireOp",EDGE,"E6.15.3"),sQuery(id+"F0.wireOp",EDGE,"E6.15.4"),sQuery(id+"F0.wireOp",EDGE,"E6.16.0"),sQuery(id+"F0.wireOp",EDGE,"E6.16.1"),sQuery(id+"F0.wireOp",EDGE,"E6.16.2"),sQuery(id+"F0.wireOp",EDGE,"E6.16.3"),sQuery(id+"F0.wireOp",EDGE,"E6.16.4"),sQuery(id+"F0.wireOp",EDGE,"E6.17.0"),sQuery(id+"F0.wireOp",EDGE,"E6.17.1"),sQuery(id+"F0.wireOp",EDGE,"E6.17.2"),sQuery(id+"F0.wireOp",EDGE,"E6.17.3"),sQuery(id+"F0.wireOp",EDGE,"E6.17.4"),sQuery(id+"F0.wireOp",EDGE,"E6.18.0"),sQuery(id+"F0.wireOp",EDGE,"E6.18.1"),sQuery(id+"F0.wireOp",EDGE,"E6.18.2"),sQuery(id+"F0.wireOp",EDGE,"E6.18.3"),sQuery(id+"F0.wireOp",EDGE,"E6.18.4"),sQuery(id+"F0.wireOp",EDGE,"E6.19.0"),sQuery(id+"F0.wireOp",EDGE,"E6.19.1"),sQuery(id+"F0.wireOp",EDGE,"E6.19.2"),sQuery(id+"F0.wireOp",EDGE,"E6.19.3"),sQuery(id+"F0.wireOp",EDGE,"E6.19.4"),sQuery(id+"F0.wireOp",EDGE,"E6.20.0"),sQuery(id+"F0.wireOp",EDGE,"E6.20.1"),sQuery(id+"F0.wireOp",EDGE,"E6.20.2"),sQuery(id+"F0.wireOp",EDGE,"E6.20.3"),sQuery(id+"F0.wireOp",EDGE,"E6.20.4"),sQuery(id+"F0.wireOp",EDGE,"E6.21.0"),sQuery(id+"F0.wireOp",EDGE,"E6.21.1"),sQuery(id+"F0.wireOp",EDGE,"E6.21.2"),sQuery(id+"F0.wireOp",EDGE,"E6.21.3"),sQuery(id+"F0.wireOp",EDGE,"E6.21.4"),sQuery(id+"F0.wireOp",EDGE,"E6.22.0"),sQuery(id+"F0.wireOp",EDGE,"E6.22.1"),sQuery(id+"F0.wireOp",EDGE,"E6.22.2"),sQuery(id+"F0.wireOp",EDGE,"E6.22.3"),sQuery(id+"F0.wireOp",EDGE,"E6.22.4"),sQuery(id+"F0.wireOp",EDGE,"E6.23.0"),sQuery(id+"F0.wireOp",EDGE,"E6.23.1"),sQuery(id+"F0.wireOp",EDGE,"E6.23.2"),sQuery(id+"F0.wireOp",EDGE,"E6.23.3"),sQuery(id+"F0.wireOp",EDGE,"E6.23.4")])],"isStart":false});
            var sketch = newSketch(context, id + "F8", { "sketchPlane" : qUnion([Q0])});
            skCircle(sketch, "E10", {"center": v(0, 0) * mm, "radius": 42.98 * mm});
            skCircle(sketch, "E11.0", {"center": v(0, 0) * mm, "radius": 34.98 * mm});
            skCircle(sketch, "E12.0", {"center": v(0, 0) * mm, "radius": 11.1 * mm});
            skCircle(sketch, "E13.0", {"center": v(0, 0) * mm, "radius": 19.1 * mm});
            skLineSegment(sketch, "E14.trimOffspring", {"start": v(5, 18.43) * mm, "end": v(5, 34.62) * mm});
            skLineSegment(sketch, "E15.trimOffspring", {"start": v(-5, 18.43) * mm, "end": v(-5, 34.62) * mm});
            skLineSegment(sketch, "E16.1.0", {"start": v(-18.43, 5) * mm, "end": v(-34.62, 5) * mm});
            skLineSegment(sketch, "E16.1.1", {"start": v(-18.43, -5) * mm, "end": v(-34.62, -5) * mm});
            skLineSegment(sketch, "E16.2.0", {"start": v(-5, -18.43) * mm, "end": v(-5, -34.62) * mm});
            skLineSegment(sketch, "E16.2.1", {"start": v(5, -18.43) * mm, "end": v(5, -34.62) * mm});
            skLineSegment(sketch, "E17.3.3.0", {"start": v(18.43, 5) * mm, "end": v(34.62, 5) * mm});
            skLineSegment(sketch, "E17.4.3.0", {"start": v(18.43, -5) * mm, "end": v(34.62, -5) * mm});
            skSolve(sketch);
        }
        {
            var Q0;
            {var subQ0=sQuery(id+"F8.wireOp",EDGE,"E15.trimOffspring");Q0=makeQuery(id+"F8.imprint","IMPRINT",FACE,{"disambiguationData":[TD([[makeQuery(id+"F8.imprint","IMPRINT",EDGE,{"derivedFrom":subQ0}),1.0]])]});}
            var Q1;
            {var subQ0=sQuery(id+"F8.wireOp",EDGE,"E14.trimOffspring");Q1=makeQuery(id+"F8.imprint","IMPRINT",FACE,{"disambiguationData":[TD([[makeQuery(id+"F8.imprint","IMPRINT",EDGE,{"derivedFrom":subQ0}),-1.0]])]});}
            var Q2;
            {var subQ0=sQuery(id+"F8.wireOp",EDGE,"E16.1.1");Q2=makeQuery(id+"F8.imprint","IMPRINT",FACE,{"disambiguationData":[TD([[makeQuery(id+"F8.imprint","IMPRINT",EDGE,{"derivedFrom":subQ0}),1.0]])]});}
            var Q3;
            {var subQ0=sQuery(id+"F8.wireOp",EDGE,"E16.2.1");Q3=makeQuery(id+"F8.imprint","IMPRINT",FACE,{"disambiguationData":[TD([[makeQuery(id+"F8.imprint","IMPRINT",EDGE,{"derivedFrom":subQ0}),1.0]])]});}
            extrude(context, id + "F9", {"entities" : qUnion([Q0, Q1, Q2, Q3]), "operationType" : NewBodyOperationType.REMOVE, "oppositeDirection" : true, "depth" : 25 * mm});
        }
    });
